# Revit family: IS_Kubo_T7174_BIM_FR
name_source: partatom
category: Plumbing Fixtures
revit_build: Autodesk Revit 2017 (Build: 20160225_1515(x64)
units: mm (PartAtom-declared; Revit-internal decimal feet)

## family parameters
Always vertical = No
Cut with Voids When Loaded = No
OmniClass Number = 23.45.05.14.21.11
OmniClass Title = Bath/Shower Units
Part Type = Normal
Room Calculation Point = No
Round Connector Dimension = Use Diameter
Shared = No
Work Plane-Based = No

## types (1)
- T7174EO - KUBO PAROI LAT FIXE 80 TSP ARG BRIL IC
    Accessoires = www.idealspec.fr
    Auteur = Ideal Standard
    BOSUseNativeGeometries = 1
    Bim-NomDuProjet = ISI_IdealStandard_ShowerEnclosures_Kubo_T7174
    Caractéristiques = KUBO Paroi de douche 80 cm verre transparent
    CodeBarre = 8014140370925
    Conformité = NF
    ConseilsDInstallation = 0
    Cost = 0 $
    Couleur = clair
    CoûtDeRemplacement = 0
    DateDeCréation = 2018_08_03
    Description = KUBO Paroi de douche 80 cm verre transparent
    DiamètreÉvacuation = 0
    Dimensions = 1950 x 22 x 744mm
    EAN code = https://8014140370925
    Espace = Interne
    Finition = clair
    Forme = rectangulaire
    Hauteur = 1950 mm
    IfcExportAs = Shower enclosures
    IfcExportType = IfcSanitaryTerminalType
    InformationsProduit = www.idealspec.fr
    Largeur = 22 mm
    Longueur = 744 mm  [stored 2.44094 ft]
    Marque = Ideal Standard
    Matériel = Glass
    Model = T7174EO
    Nom = ShowerEnclosures_Kubo_T7174_IdealStandard
    PoidsNet = 23,50 KG
    Profondeur = 0 mm  [stored 0 ft]
    Raccordement = Plomberie
    Receveur = No
    Révision = 1
    URL = www.idealspec.fr
    Uniclass2015Code = Pr_40_20_06_79
    Uniclass2015Title = Shower enclosures
    Uniclass2015Version = Products v1.1
    UnitéDeMesure = Millimètres
    UnitéDeTemps = An
    UnitéMonétaire = €
    UrlDuFabricant = www.idealspec.fr
    Version = 1

note: [stored X ft] marks values corroborated as IEEE doubles in the binary element streams (Revit-internal decimal feet)

## geometry (parser evidence)
native form markers: Sweep x2
no freeform markers — native parametric forms only
